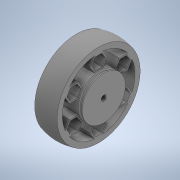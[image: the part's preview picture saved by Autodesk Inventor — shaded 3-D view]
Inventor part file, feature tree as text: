
AUTODESK INVENTOR PART (.ipt)
format: ipt  version: 2020 (Build 240168000, 168)  size: 305,664 bytes
history: native  units: in
note: dims shown in document units (in); Inventor stores cm internally (conversion verified against a paired STEP export)
features: sketch x4, extrude x2, revolve x2, projected_geometry x1
ambient origin geometry x8: Origin, YZ Plane, XZ Plane, XY Plane, X Axis, Y Axis, Z Axis, Center Point
bodies: Solid1 (feature_tree)
feature tree (9):
  extrude  "Extrusion1"  Depth=0.1181in
  sketch  "Sketch3"  dims[d6=0.9843in d7=0.1181in]
  revolve  "Revolution1"  [1 undecoded]
  extrude  "Extrusion2"  Depth=0.1181in
  revolve  "Revolution2"  [1 undecoded]
  sketch  "Sketch1"  dims[d0=0.1181in d1=0.0394in]
  sketch  "Sketch2"  dims[d3=1.8898in d4=0.1181in]
  projected_geometry  "Projected Loop1"
  sketch  "Sketch4"  dims[d8=0.0in d9=1.8898in d10=0.1181in d11=0.0315in d12=2.3622in d14=360.0deg d16=0.5118in d17=0.0in d19=90.0deg d20=0.0394in d22=60.0deg d24=0.0394in d25=90.0deg d26=60.0deg]
note: 2 required parameter values undecoded (feature->parameter linkage not recoverable at this tier; creation-order binding heuristic only, values carry confidence <= 0.55)
